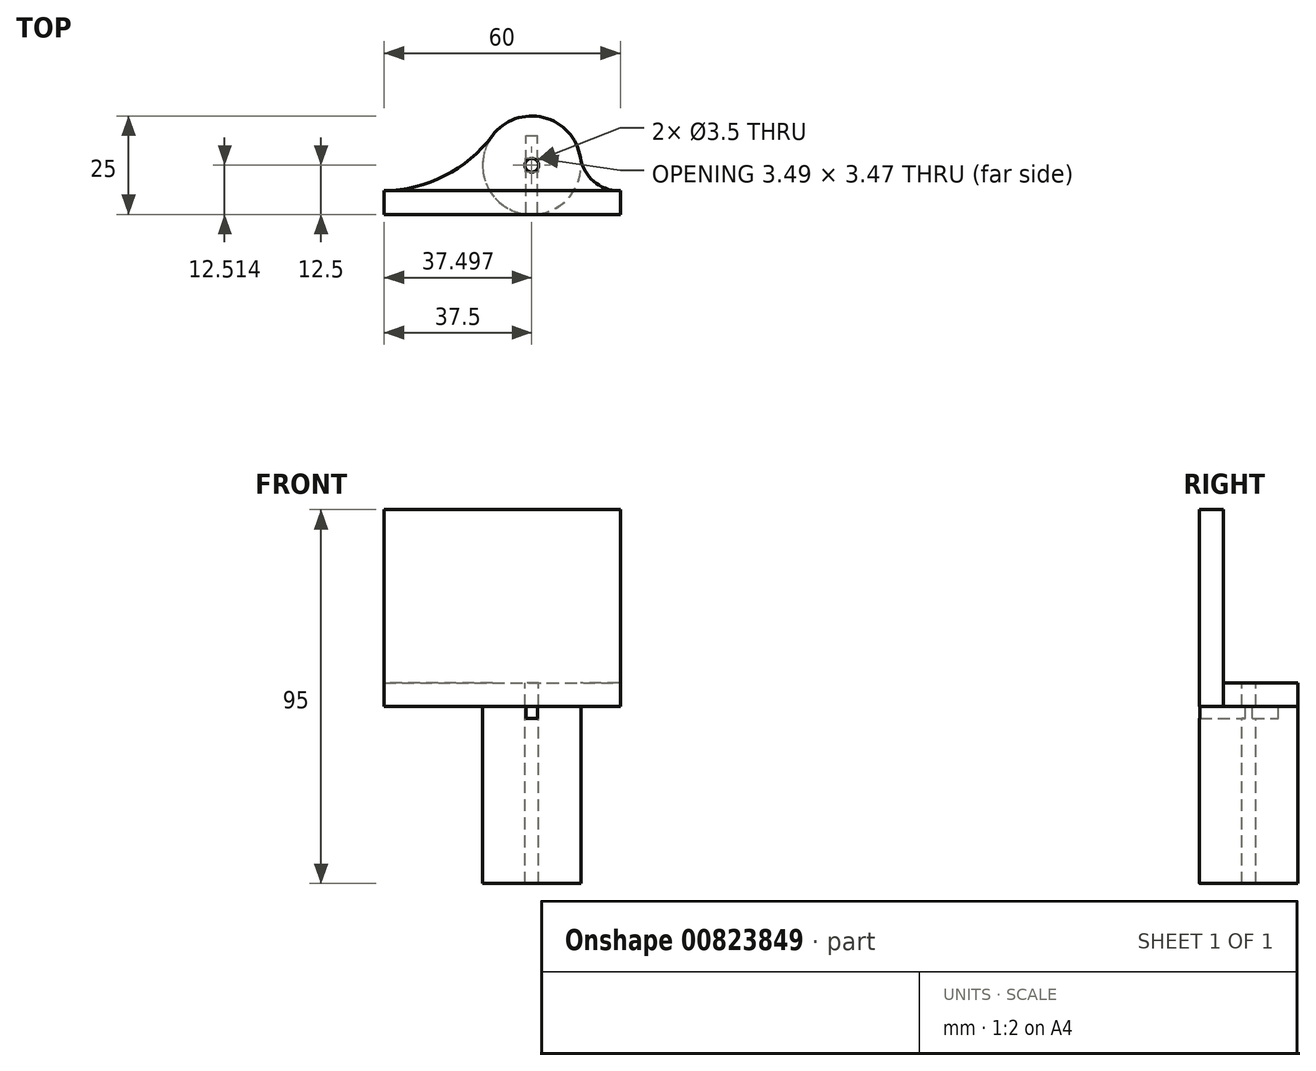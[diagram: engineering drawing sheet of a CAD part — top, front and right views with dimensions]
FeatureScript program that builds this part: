
annotation { "Feature Type Name" : "Feature", "Feature Type Description" : "" }
export const myFeature = defineFeature(function(context is Context, id is Id, definition is map)
    precondition{}
    {
        {
            var Q0;
            Q0=qCreatedBy(makeId("Front.planeOp"),FACE);
            var sketch = newSketch(context, id + "F0", { "sketchPlane" : qUnion([Q0])});
            skLineSegment(sketch, "E0.bottom", {"start": v(0, 0) * mm, "end": v(-60, 0) * mm});
            skLineSegment(sketch, "E0.top", {"start": v(0, 50) * mm, "end": v(-60, 50) * mm});
            skLineSegment(sketch, "E0.left", {"start": v(0, 0) * mm, "end": v(0, 50) * mm});
            skLineSegment(sketch, "E0.right", {"start": v(-60, 0) * mm, "end": v(-60, 50) * mm});
            skSolve(sketch);
        }
        {
            var Q0;
            Q0 = qSketchRegion(id + "F0", true);
            extrude(context, id + "F1", {"entities" : qUnion([Q0]), "depth" : 6 * mm, "offsetDistance" : 25 * mm});
        }
        {
            var Q0;
            Q0=makeQuery(id+"F1.opExtrude","SWEPT_FACE",FACE,{"disambiguationData":[OSD([sQuery(id+"F0.wireOp",EDGE,"E0.bottom")])]});
            var sketch = newSketch(context, id + "F2", { "sketchPlane" : qUnion([Q0])});
            skCircle(sketch, "E1", {"center": v(-22.5, -6.5) * mm, "radius": 12.5 * mm});
            skSolve(sketch);
        }
        {
            var Q0;
            Q0 = qSketchRegion(id + "F2", true);
            extrude(context, id + "F3", {"entities" : qUnion([Q0]), "operationType" : NewBodyOperationType.ADD, "oppositeDirection" : true, "depth" : 6 * mm, "offsetDistance" : 25 * mm});
        }
        {
            var Q0;
            {var subQ0=sQuery(id+"F2.wireOp",EDGE,"E1");var subQ1=makeQuery(id+"F1.opExtrude","CAP_EDGE",EDGE,{"disambiguationData":[OSD([sQuery(id+"F0.wireOp",EDGE,"E0.bottom")])],"isStart":true});var subQ2=makeQuery(id+"F2.imprint","INTERSECT",VERTEX,{"disambiguationData":[OD(0.0)],"derivedFrom":[subQ1,subQ0]});Q0=makeQuery(id+"F2.imprint","IMPRINT",FACE,{"disambiguationData":[TD([[makeQuery(id+"F2.imprint","IMPRINT",EDGE,{"disambiguationData":[TD([[subQ2,1.0]])],"derivedFrom":subQ0}),1.0]])]});}
            var sketch = newSketch(context, id + "F4", { "sketchPlane" : qUnion([Q0])});
            skLineSegment(sketch, "E2.bottom", {"start": v(-24, 6) * mm, "end": v(-21, 6) * mm});
            skLineSegment(sketch, "E2.top", {"start": v(-24, -14) * mm, "end": v(-21, -14) * mm});
            skLineSegment(sketch, "E2.left", {"start": v(-24, 6) * mm, "end": v(-24, -14) * mm});
            skLineSegment(sketch, "E2.right", {"start": v(-21, 6) * mm, "end": v(-21, -14) * mm});
            skSolve(sketch);
        }
        {
            var Q0;
            Q0 = qSketchRegion(id + "F4", true);
            extrude(context, id + "F5", {"entities" : qUnion([Q0]), "operationType" : NewBodyOperationType.ADD, "depth" : 3 * mm, "offsetDistance" : 25 * mm});
        }
        {
            var Q0;
            {var subQ1=sQuery(id+"F4.wireOp",EDGE,"E2.top");Q0=makeQuery(id+"F4.imprint","IMPRINT",FACE,{"disambiguationData":[TD([[makeQuery(id+"F4.imprint","IMPRINT",EDGE,{"derivedFrom":subQ1}),-1.0]])]});}
            var sketch = newSketch(context, id + "F6", { "sketchPlane" : qUnion([Q0])});
            skCircle(sketch, "E3", {"center": v(-22.5, -6.5) * mm, "radius": 12.5 * mm});
            skSolve(sketch);
        }
        {
            var Q0;
            Q0 = qSketchRegion(id + "F6", true);
            extrude(context, id + "F7", {"entities" : qUnion([Q0]), "depth" : 45 * mm, "offsetDistance" : 25 * mm});
        }
        {
            var Q0;
            Q0=makeQuery(id+"F3.opExtrude","CAP_FACE",FACE,{"disambiguationData":[OSD([sQuery(id+"F2.wireOp",EDGE,"E1")])],"isStart":false});
            var sketch = newSketch(context, id + "F8", { "sketchPlane" : qUnion([Q0])});
            skCircle(sketch, "E4", {"center": v(-22.5, 6.5) * mm, "radius": 1.75 * mm});
            skSolve(sketch);
        }
        {
            var Q0;
            Q0 = qSketchRegion(id + "F8", true);
            extrude(context, id + "F9", {"entities" : qUnion([Q0]), "operationType" : NewBodyOperationType.REMOVE, "endBound" : BoundingType.THROUGH_ALL, "oppositeDirection" : true, "depth" : 25 * mm, "offsetDistance" : 25 * mm});
        }
        {
            var Q0;
            Q0=makeQuery(id+"F3.boolean.opBoolean","INTERSECT",EDGE,{"disambiguationData":[OD(1.0)],"derivedFrom":[makeQuery(id+"F1.opExtrude","CAP_FACE",FACE,{"disambiguationData":[OSD([sQuery(id+"F0.wireOp",EDGE,"E0.bottom"),sQuery(id+"F0.wireOp",EDGE,"E0.top"),sQuery(id+"F0.wireOp",EDGE,"E0.left"),sQuery(id+"F0.wireOp",EDGE,"E0.right")])],"isStart":true}),makeQuery(id+"F3.opExtrude","SWEPT_FACE",FACE,{"disambiguationData":[OSD([sQuery(id+"F2.wireOp",EDGE,"E1")])]})]});
            fillet(context, id + "F10", {"entities" : qUnion([Q0]), "radius" : 35 * mm, "tangentPropagation" : true, "allowEdgeOverflow" : false});
        }
        {
            var Q0;
            Q0=makeQuery(id+"F3.boolean.opBoolean","INTERSECT",EDGE,{"disambiguationData":[OD(0.0)],"derivedFrom":[makeQuery(id+"F1.opExtrude","CAP_FACE",FACE,{"disambiguationData":[OSD([sQuery(id+"F0.wireOp",EDGE,"E0.bottom"),sQuery(id+"F0.wireOp",EDGE,"E0.top"),sQuery(id+"F0.wireOp",EDGE,"E0.left"),sQuery(id+"F0.wireOp",EDGE,"E0.right")])],"isStart":true}),makeQuery(id+"F3.opExtrude","SWEPT_FACE",FACE,{"disambiguationData":[OSD([sQuery(id+"F2.wireOp",EDGE,"E1")])]})]});
            fillet(context, id + "F11", {"entities" : qUnion([Q0]), "radius" : 10 * mm, "tangentPropagation" : true, "allowEdgeOverflow" : false});
        }
        {
            var Q0;
            Q0 = qSketchRegion(id + "F4", true);
            extrude(context, id + "F12", {"entities" : qUnion([Q0]), "operationType" : NewBodyOperationType.REMOVE, "depth" : 3 * mm, "offsetDistance" : 25 * mm});
        }
    });
